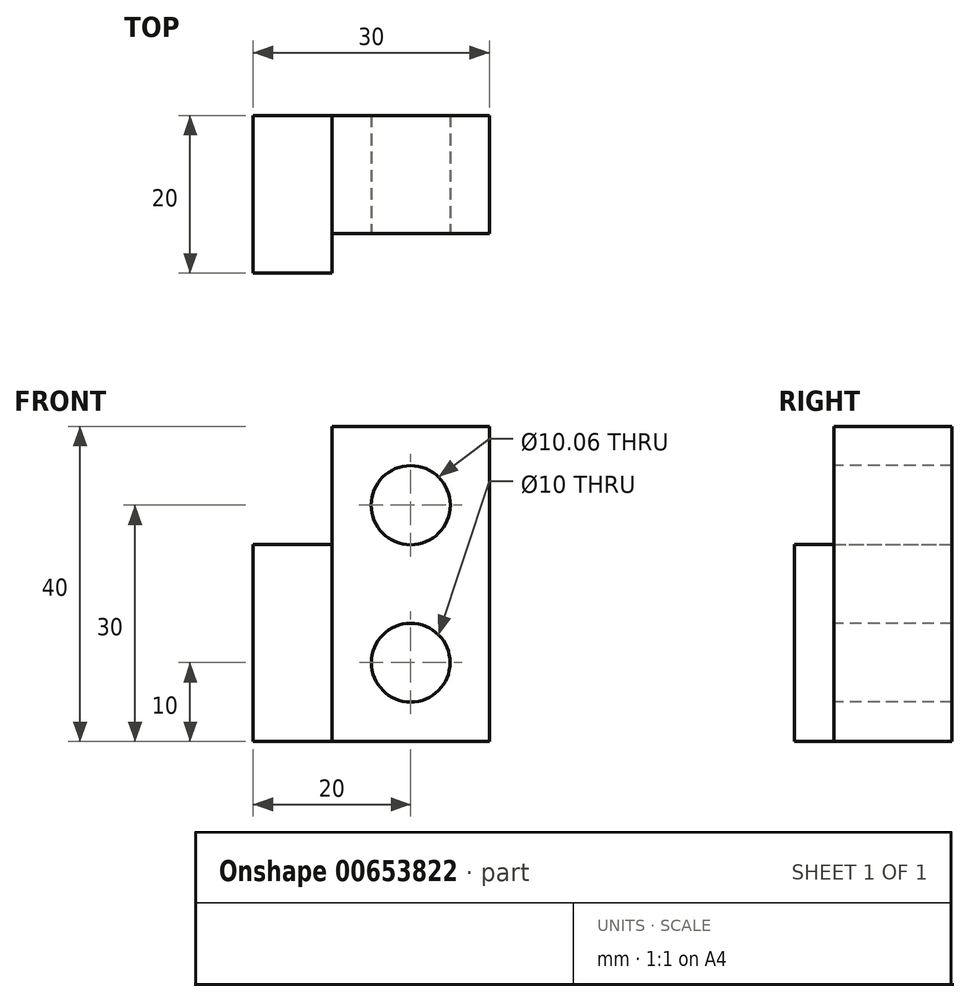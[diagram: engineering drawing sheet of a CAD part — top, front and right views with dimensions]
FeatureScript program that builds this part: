
annotation { "Feature Type Name" : "Feature", "Feature Type Description" : "" }
export const myFeature = defineFeature(function(context is Context, id is Id, definition is map)
    precondition{}
    {
        {
            var Q0;
            Q0=qCreatedBy(makeId("Front.planeOp"),FACE);
            var sketch = newSketch(context, id + "F0", { "sketchPlane" : qUnion([Q0])});
            skLineSegment(sketch, "E0.bottom", {"start": v(0, 0) * mm, "end": v(-10, 0) * mm});
            skLineSegment(sketch, "E0.top", {"start": v(0, 25) * mm, "end": v(-10, 25) * mm});
            skLineSegment(sketch, "E0.left", {"start": v(0, 0) * mm, "end": v(0, 25) * mm});
            skLineSegment(sketch, "E0.right", {"start": v(-10, 0) * mm, "end": v(-10, 25) * mm});
            skLineSegment(sketch, "E1.bottom", {"start": v(20, 40) * mm, "end": v(0, 40) * mm});
            skLineSegment(sketch, "E1.top", {"start": v(20, 0) * mm, "end": v(0, 0) * mm});
            skLineSegment(sketch, "E1.left", {"start": v(20, 40) * mm, "end": v(20, 0) * mm});
            skLineSegment(sketch, "E1.right", {"start": v(0, 40) * mm, "end": v(0, 0) * mm});
            skSolve(sketch);
        }
        {
            var Q0;
            {var subQ2=sQuery(id+"F0.wireOp",EDGE,"E1.bottom");Q0=makeQuery(id+"F0.imprint","IMPRINT",FACE,{"disambiguationData":[TD([[makeQuery(id+"F0.imprint","IMPRINT",EDGE,{"derivedFrom":subQ2}),1.0]])]});}
            extrude(context, id + "F1", {"entities" : qUnion([Q0]), "depth" : 15 * mm, "offsetDistance" : 25 * mm});
        }
        {
            var Q0;
            {var subQ0=sQuery(id+"F0.wireOp",EDGE,"E0.bottom");Q0=makeQuery(id+"F0.imprint","IMPRINT",FACE,{"disambiguationData":[TD([[makeQuery(id+"F0.imprint","IMPRINT",EDGE,{"derivedFrom":subQ0}),-1.0]])]});}
            extrude(context, id + "F2", {"entities" : qUnion([Q0]), "operationType" : NewBodyOperationType.ADD, "depth" : 20 * mm, "offsetDistance" : 25 * mm});
        }
        {
            var Q0;
            Q0=makeQuery(id+"F1.opExtrude","CAP_FACE",FACE,{"disambiguationData":[OSD([sQuery(id+"F0.wireOp",EDGE,"E1.bottom"),sQuery(id+"F0.wireOp",EDGE,"E1.top"),sQuery(id+"F0.wireOp",EDGE,"E1.left"),sQuery(id+"F0.wireOp",EDGE,"E1.right")])],"isStart":false});
            var sketch = newSketch(context, id + "F3", { "sketchPlane" : qUnion([Q0])});
            skCircle(sketch, "E2", {"center": v(10, 10) * mm, "radius": 5 * mm});
            skCircle(sketch, "E3", {"center": v(10, 30) * mm, "radius": 5.03 * mm});
            skSolve(sketch);
        }
        {
            var Q0;
            Q0=makeQuery(id+"F3.imprint","IMPRINT",FACE,{"disambiguationData":[TD([[makeQuery(id+"F3.imprint","IMPRINT",EDGE,{"derivedFrom":sQuery(id+"F3.wireOp",EDGE,"E2")}),1.0]])]});
            var Q1;
            Q1=makeQuery(id+"F3.imprint","IMPRINT",FACE,{"disambiguationData":[TD([[makeQuery(id+"F3.imprint","IMPRINT",EDGE,{"derivedFrom":sQuery(id+"F3.wireOp",EDGE,"E3")}),1.0]])]});
            extrude(context, id + "F4", {"entities" : qUnion([Q0, Q1]), "operationType" : NewBodyOperationType.REMOVE, "oppositeDirection" : true, "depth" : 15 * mm, "offsetDistance" : 25 * mm});
        }
    });
